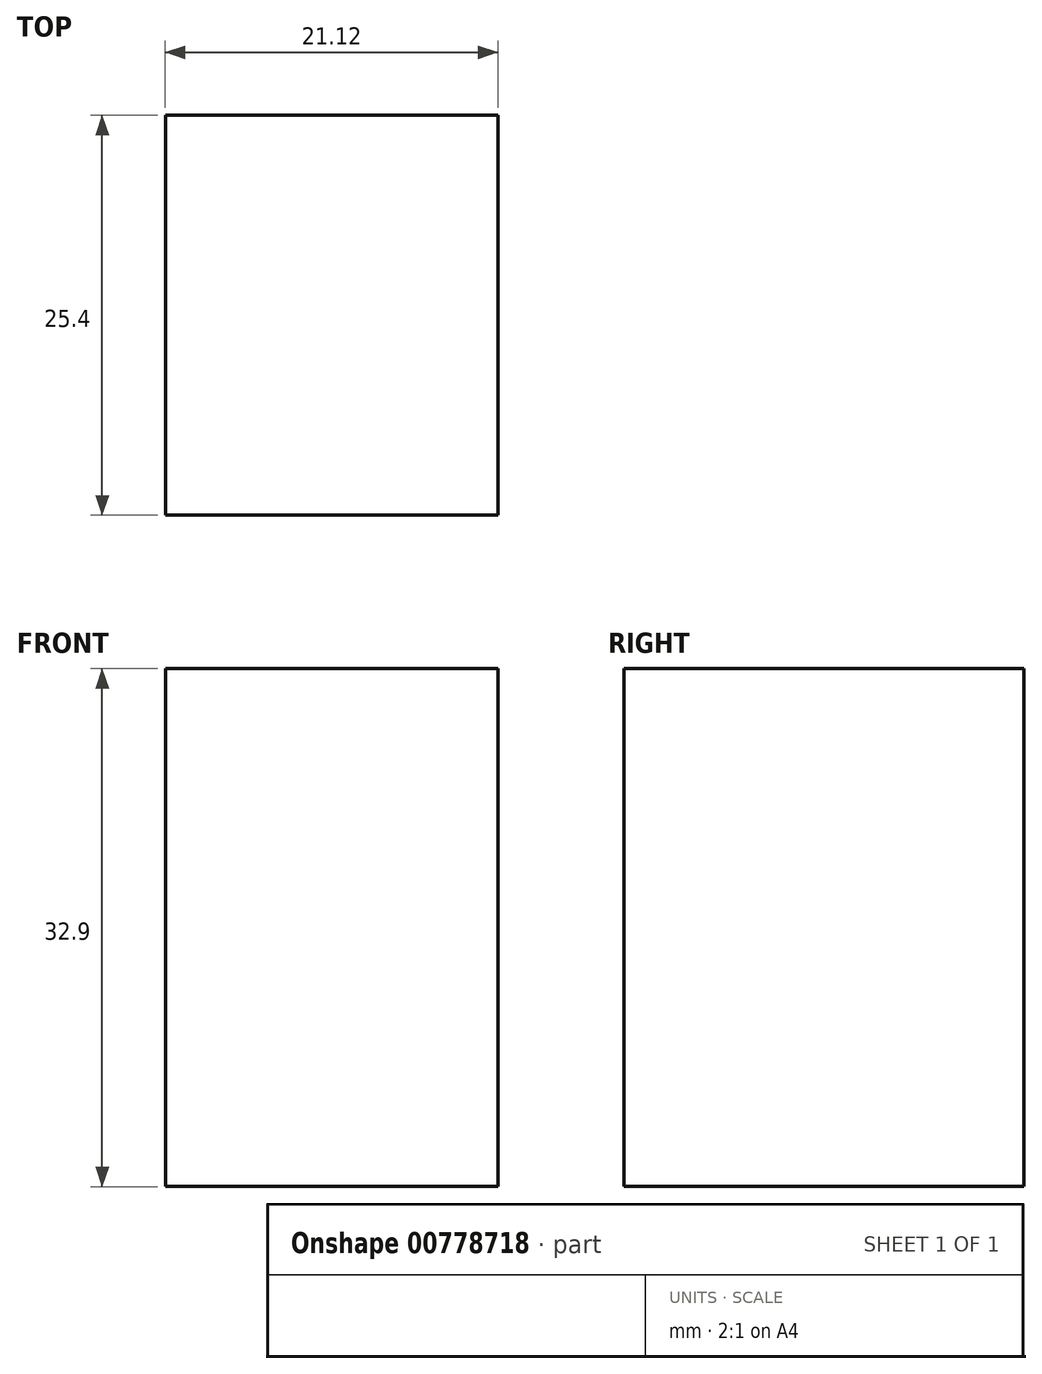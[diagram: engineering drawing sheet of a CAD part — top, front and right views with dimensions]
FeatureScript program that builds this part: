
annotation { "Feature Type Name" : "Feature", "Feature Type Description" : "" }
export const myFeature = defineFeature(function(context is Context, id is Id, definition is map)
    precondition{}
    {
        {
            var Q0;
            Q0=qCreatedBy(makeId("Front.planeOp"),FACE);
            var sketch = newSketch(context, id + "F0", { "sketchPlane" : qUnion([Q0])});
            skLineSegment(sketch, "E0.bottom", {"start": v(-9.65, 5.38) * mm, "end": v(11.47, 5.38) * mm});
            skLineSegment(sketch, "E0.top", {"start": v(-9.65, -27.52) * mm, "end": v(11.47, -27.52) * mm});
            skLineSegment(sketch, "E0.left", {"start": v(-9.65, 5.38) * mm, "end": v(-9.65, -27.52) * mm});
            skLineSegment(sketch, "E0.right", {"start": v(11.47, 5.38) * mm, "end": v(11.47, -27.52) * mm});
            skSolve(sketch);
        }
        {
            var Q0;
            Q0=makeQuery(id+"F0.imprint","IMPRINT",FACE,{"disambiguationData":[TD([[makeQuery(id+"F0.imprint","IMPRINT",EDGE,{"derivedFrom":sQuery(id+"F0.wireOp",EDGE,"E0.bottom")}),-1.0]])]});
            extrude(context, id + "F1", {"entities" : qUnion([Q0]), "depth" : 25.4 * mm, "offsetDistance" : 25.4 * mm});
        }
    });
